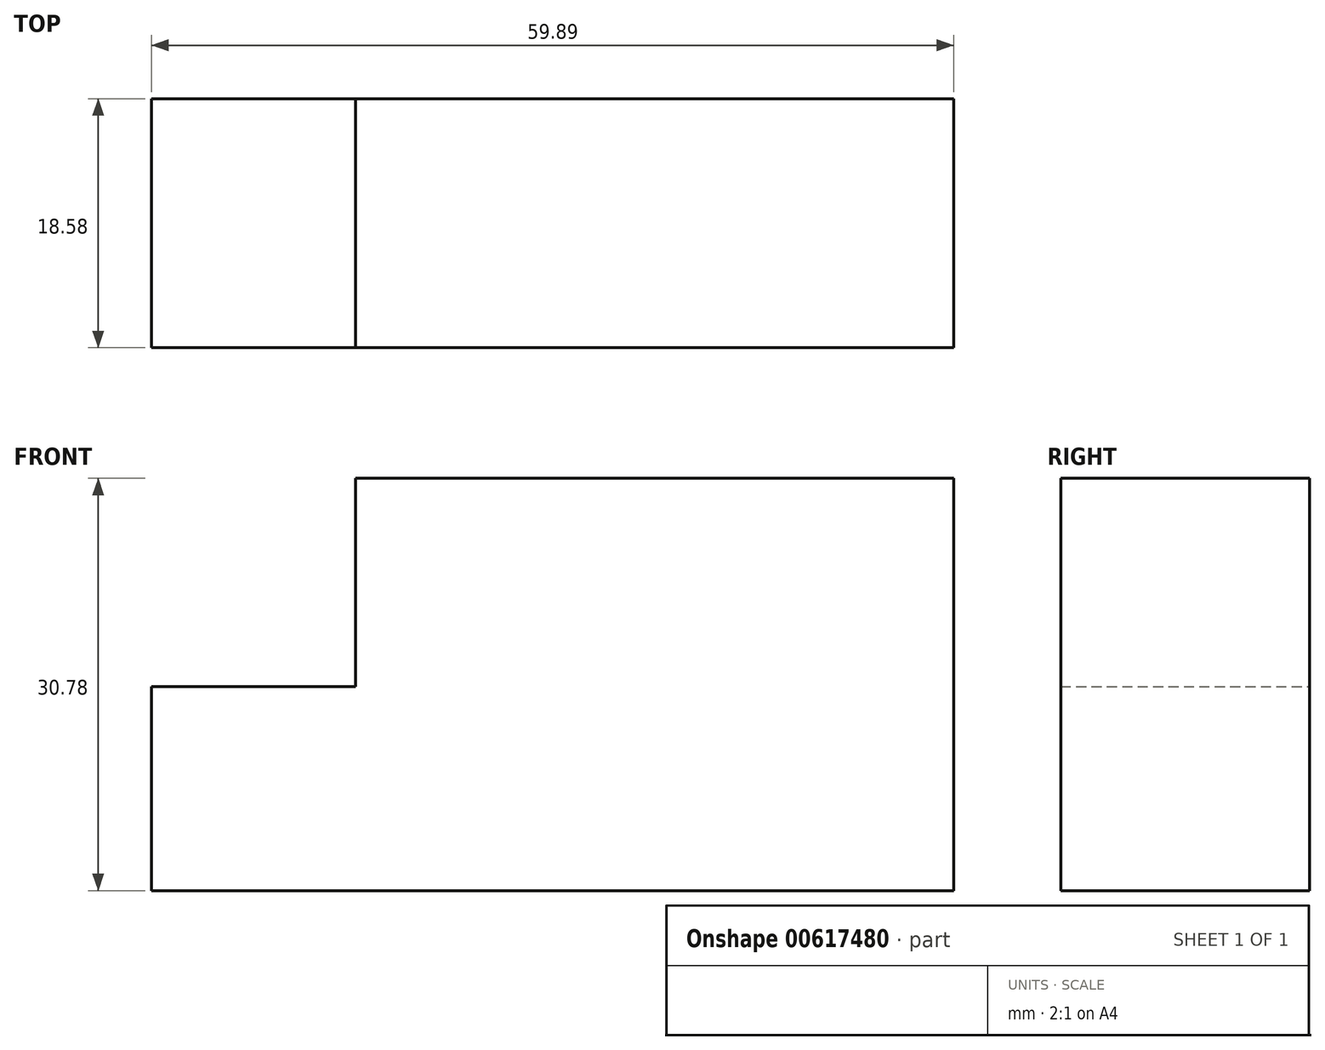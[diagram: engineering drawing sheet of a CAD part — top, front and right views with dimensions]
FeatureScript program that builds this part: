
annotation { "Feature Type Name" : "Feature", "Feature Type Description" : "" }
export const myFeature = defineFeature(function(context is Context, id is Id, definition is map)
    precondition{}
    {
        {
            var Q0;
            Q0=qCreatedBy(makeId("Front.planeOp"),FACE);
            var sketch = newSketch(context, id + "F0", { "sketchPlane" : qUnion([Q0])});
            skLineSegment(sketch, "E0", {"start": v(0, 0) * mm, "end": v(-59.9, 0) * mm});
            skLineSegment(sketch, "E1", {"start": v(-59.9, 0) * mm, "end": v(-59.9, 15.24) * mm});
            skLineSegment(sketch, "E2", {"start": v(-59.9, 15.24) * mm, "end": v(-44.65, 15.24) * mm});
            skLineSegment(sketch, "E3", {"start": v(-44.65, 15.24) * mm, "end": v(-44.65, 30.78) * mm});
            skLineSegment(sketch, "E4", {"start": v(-44.65, 30.78) * mm, "end": v(0, 30.78) * mm});
            skLineSegment(sketch, "E5", {"start": v(0, 30.78) * mm, "end": v(0, 0) * mm});
            skSolve(sketch);
        }
        {
            var Q0;
            Q0=makeQuery(id+"F0.imprint","IMPRINT",FACE,{"disambiguationData":[TD([[makeQuery(id+"F0.imprint","IMPRINT",EDGE,{"derivedFrom":sQuery(id+"F0.wireOp",EDGE,"E0")}),-1.0]])]});
            extrude(context, id + "F1", {"entities" : qUnion([Q0]), "depth" : 18.58 * mm, "offsetDistance" : 25.4 * mm});
        }
    });
